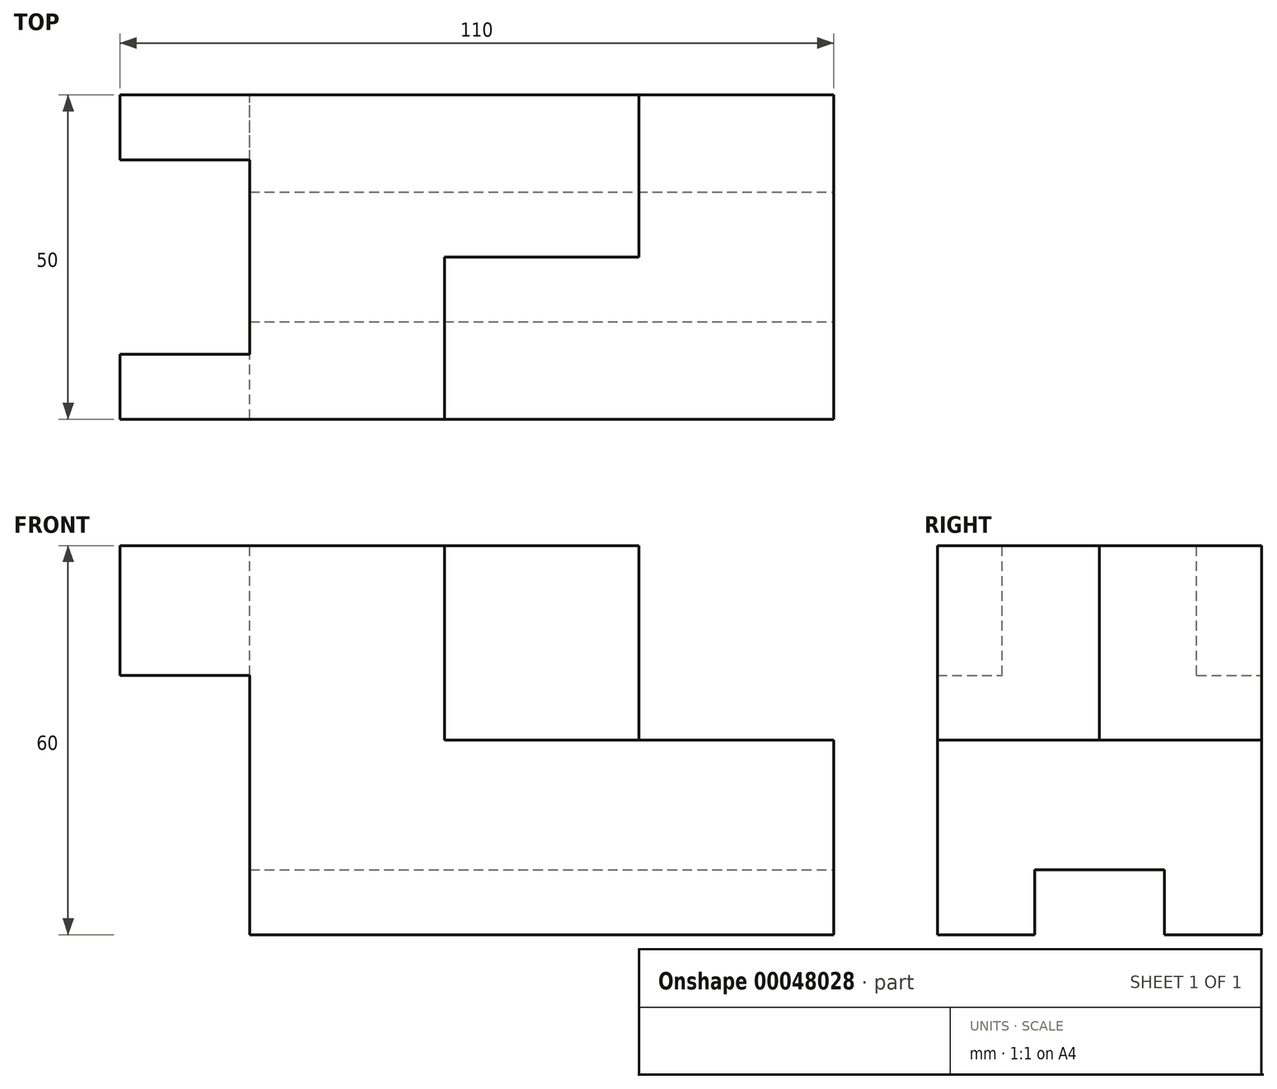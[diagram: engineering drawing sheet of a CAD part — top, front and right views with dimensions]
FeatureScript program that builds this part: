
annotation { "Feature Type Name" : "Feature", "Feature Type Description" : "" }
export const myFeature = defineFeature(function(context is Context, id is Id, definition is map)
    precondition{}
    {
        {
            var Q0;
            Q0=qCreatedBy(makeId("Front.planeOp"),FACE);
            var sketch = newSketch(context, id + "F0", { "sketchPlane" : qUnion([Q0])});
            skLineSegment(sketch, "E0", {"start": v(0, 0) * mm, "end": v(90, 0) * mm});
            skLineSegment(sketch, "E1", {"start": v(90, 0) * mm, "end": v(90, 30) * mm});
            skLineSegment(sketch, "E2", {"start": v(90, 30) * mm, "end": v(30, 30) * mm});
            skLineSegment(sketch, "E3", {"start": v(30, 30) * mm, "end": v(30, 60) * mm});
            skLineSegment(sketch, "E4", {"start": v(30, 60) * mm, "end": v(-20, 60) * mm});
            skLineSegment(sketch, "E5", {"start": v(-20, 60) * mm, "end": v(-20, 40) * mm});
            skLineSegment(sketch, "E6", {"start": v(-20, 40) * mm, "end": v(0, 40) * mm});
            skLineSegment(sketch, "E7", {"start": v(0, 40) * mm, "end": v(0, 0) * mm});
            skLineSegment(sketch, "E8", {"start": v(30, 60) * mm, "end": v(60, 60) * mm});
            skLineSegment(sketch, "E9", {"start": v(60, 60) * mm, "end": v(60, 30) * mm});
            skSolve(sketch);
        }
        {
            var Q0;
            Q0=makeQuery(id+"F0.imprint","IMPRINT",FACE,{"disambiguationData":[TD([[makeQuery(id+"F0.imprint","IMPRINT",EDGE,{"derivedFrom":sQuery(id+"F0.wireOp",EDGE,"E0")}),1.0]])]});
            extrude(context, id + "F1", {"entities" : qUnion([Q0]), "depth" : 50 * mm});
        }
        {
            var Q0;
            {var subQ1=sQuery(id+"F0.wireOp",EDGE,"E3");Q0=makeQuery(id+"F0.imprint","IMPRINT",FACE,{"disambiguationData":[TD([[makeQuery(id+"F0.imprint","IMPRINT",EDGE,{"derivedFrom":subQ1}),-1.0]])]});}
            extrude(context, id + "F2", {"entities" : qUnion([Q0]), "operationType" : NewBodyOperationType.ADD, "depth" : 25 * mm});
        }
        {
            var Q0;
            Q0=makeQuery(id+"F2.boolean.opBoolean","MERGE",FACE,{"derivedFrom":[makeQuery(id+"F1.opExtrude","SWEPT_FACE",FACE,{"disambiguationData":[OSD([sQuery(id+"F0.wireOp",EDGE,"E4")])]}),makeQuery(id+"F2.opExtrude","SWEPT_FACE",FACE,{"disambiguationData":[OSD([sQuery(id+"F0.wireOp",EDGE,"E8")])]})]});
            var sketch = newSketch(context, id + "F3", { "sketchPlane" : qUnion([Q0])});
            skLineSegment(sketch, "E10", {"start": v(-20, -40) * mm, "end": v(0, -40) * mm});
            skLineSegment(sketch, "E11", {"start": v(0, -40) * mm, "end": v(0, -10) * mm});
            skLineSegment(sketch, "E12", {"start": v(0, -10) * mm, "end": v(-20, -10) * mm});
            skLineSegment(sketch, "E13", {"start": v(-20, -10) * mm, "end": v(-20, -40) * mm});
            skSolve(sketch);
        }
        {
            var Q0;
            Q0=makeQuery(id+"F3.imprint","IMPRINT",FACE,{"disambiguationData":[TD([[makeQuery(id+"F3.imprint","IMPRINT",EDGE,{"derivedFrom":sQuery(id+"F3.wireOp",EDGE,"E10")}),1.0]])]});
            extrude(context, id + "F4", {"entities" : qUnion([Q0]), "operationType" : NewBodyOperationType.REMOVE, "endBound" : BoundingType.THROUGH_ALL, "oppositeDirection" : true, "depth" : 25 * mm});
        }
        {
            var Q0;
            Q0=makeQuery(id+"F1.opExtrude","SWEPT_FACE",FACE,{"disambiguationData":[OSD([sQuery(id+"F0.wireOp",EDGE,"E1")])]});
            var sketch = newSketch(context, id + "F5", { "sketchPlane" : qUnion([Q0])});
            skLineSegment(sketch, "E14", {"start": v(-35, 0) * mm, "end": v(-35, 10) * mm});
            skLineSegment(sketch, "E15", {"start": v(-35, 10) * mm, "end": v(-15, 10) * mm});
            skLineSegment(sketch, "E16", {"start": v(-15, 10) * mm, "end": v(-15, 0) * mm});
            skLineSegment(sketch, "E17", {"start": v(-15, 0) * mm, "end": v(-35, 0) * mm});
            skSolve(sketch);
        }
        {
            var Q0;
            Q0=makeQuery(id+"F5.imprint","IMPRINT",FACE,{"disambiguationData":[TD([[makeQuery(id+"F5.imprint","IMPRINT",EDGE,{"derivedFrom":sQuery(id+"F5.wireOp",EDGE,"E14")}),-1.0]])]});
            extrude(context, id + "F6", {"entities" : qUnion([Q0]), "operationType" : NewBodyOperationType.REMOVE, "endBound" : BoundingType.THROUGH_ALL, "oppositeDirection" : true, "depth" : 25 * mm});
        }
    });
